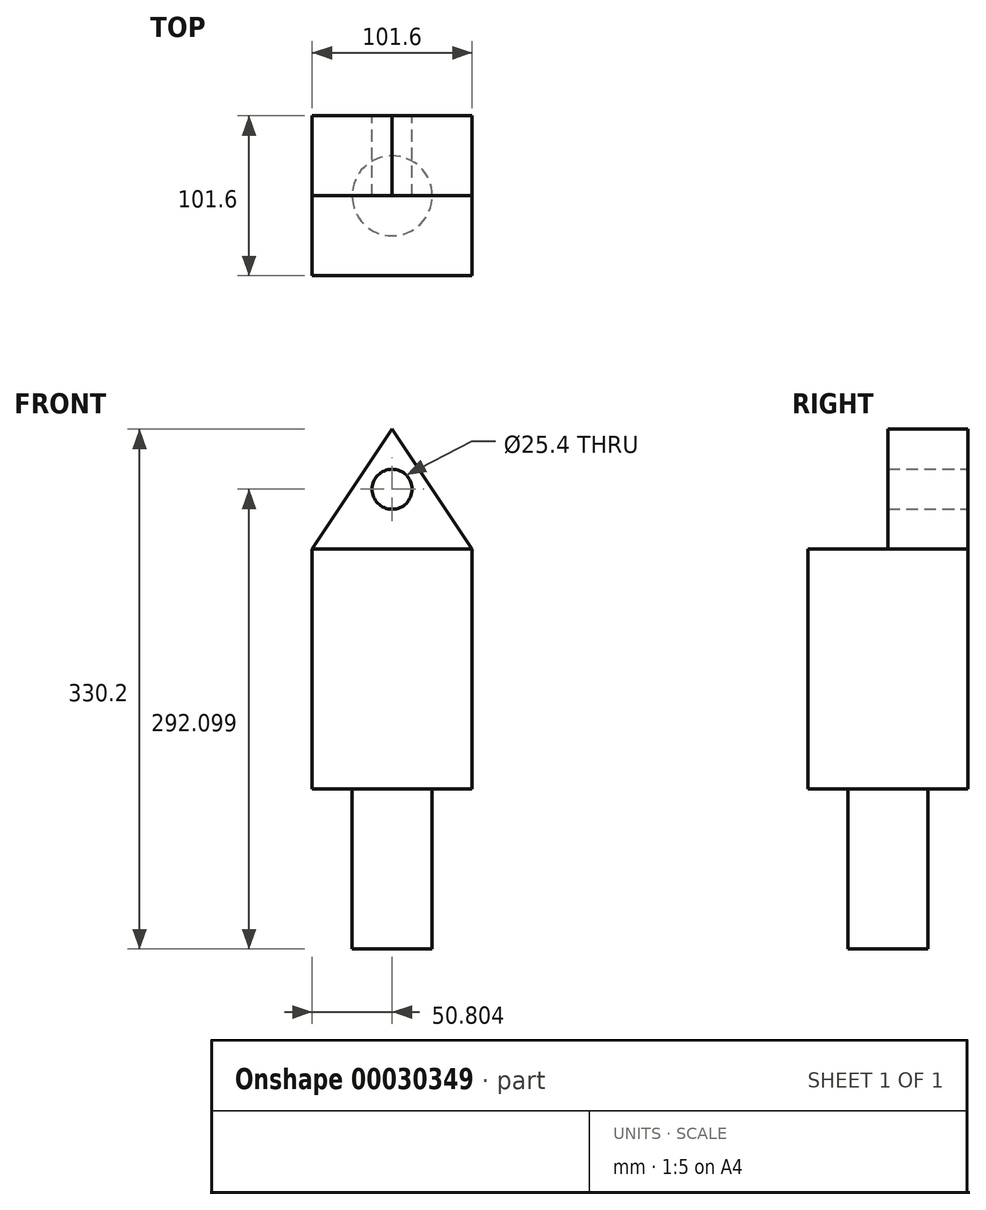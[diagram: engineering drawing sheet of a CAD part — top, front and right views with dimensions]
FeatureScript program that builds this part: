
annotation { "Feature Type Name" : "Feature", "Feature Type Description" : "" }
export const myFeature = defineFeature(function(context is Context, id is Id, definition is map)
    precondition{}
    {
        {
            var Q0;
            Q0=qCreatedBy(makeId("Front.planeOp"),FACE);
            var sketch = newSketch(context, id + "F0", { "sketchPlane" : qUnion([Q0])});
            skLineSegment(sketch, "E0.bottom", {"start": v(-20.5, 168.6) * mm, "end": v(81.1, 168.6) * mm});
            skLineSegment(sketch, "E0.top", {"start": v(-20.5, 16.2) * mm, "end": v(81.1, 16.2) * mm});
            skLineSegment(sketch, "E0.left", {"start": v(-20.5, 168.6) * mm, "end": v(-20.5, 16.2) * mm});
            skLineSegment(sketch, "E0.right", {"start": v(81.1, 168.6) * mm, "end": v(81.1, 16.2) * mm});
            skLineSegment(sketch, "E1", {"start": v(30.3, 168.6) * mm, "end": v(30.3, 244.8) * mm});
            skLineSegment(sketch, "E2", {"start": v(30.3, 244.8) * mm, "end": v(-20.5, 168.6) * mm});
            skLineSegment(sketch, "E3", {"start": v(30.3, 244.8) * mm, "end": v(81.1, 168.6) * mm});
            skCircle(sketch, "E4", {"center": v(30.3, 206.7) * mm, "radius": 12.7 * mm});
            skSolve(sketch);
        }
        {
            var Q0;
            Q0=makeQuery(id+"F0.imprint","IMPRINT",FACE,{"disambiguationData":[TD([[makeQuery(id+"F0.imprint","IMPRINT",EDGE,{"derivedFrom":sQuery(id+"F0.wireOp",EDGE,"E0.top")}),1.0]])]});
            extrude(context, id + "F1", {"entities" : qUnion([Q0]), "depth" : 101.6 * mm});
        }
        {
            var Q0;
            Q0 = qSketchRegion(id + "F0", true);
            extrude(context, id + "F2", {"entities" : qUnion([Q0]), "operationType" : NewBodyOperationType.ADD, "depth" : 50.8 * mm});
        }
        {
            var Q0;
            Q0=makeQuery(id+"F1.opExtrude","SWEPT_FACE",FACE,{"disambiguationData":[OSD([sQuery(id+"F0.wireOp",EDGE,"E0.top")])]});
            var sketch = newSketch(context, id + "F3", { "sketchPlane" : qUnion([Q0])});
            skCircle(sketch, "E5", {"center": v(30.3, 50.8) * mm, "radius": 25.4 * mm});
            skSolve(sketch);
        }
        {
            var Q0;
            Q0 = qSketchRegion(id + "F3", true);
            extrude(context, id + "F4", {"entities" : qUnion([Q0]), "operationType" : NewBodyOperationType.ADD, "depth" : 101.6 * mm});
        }
    });
